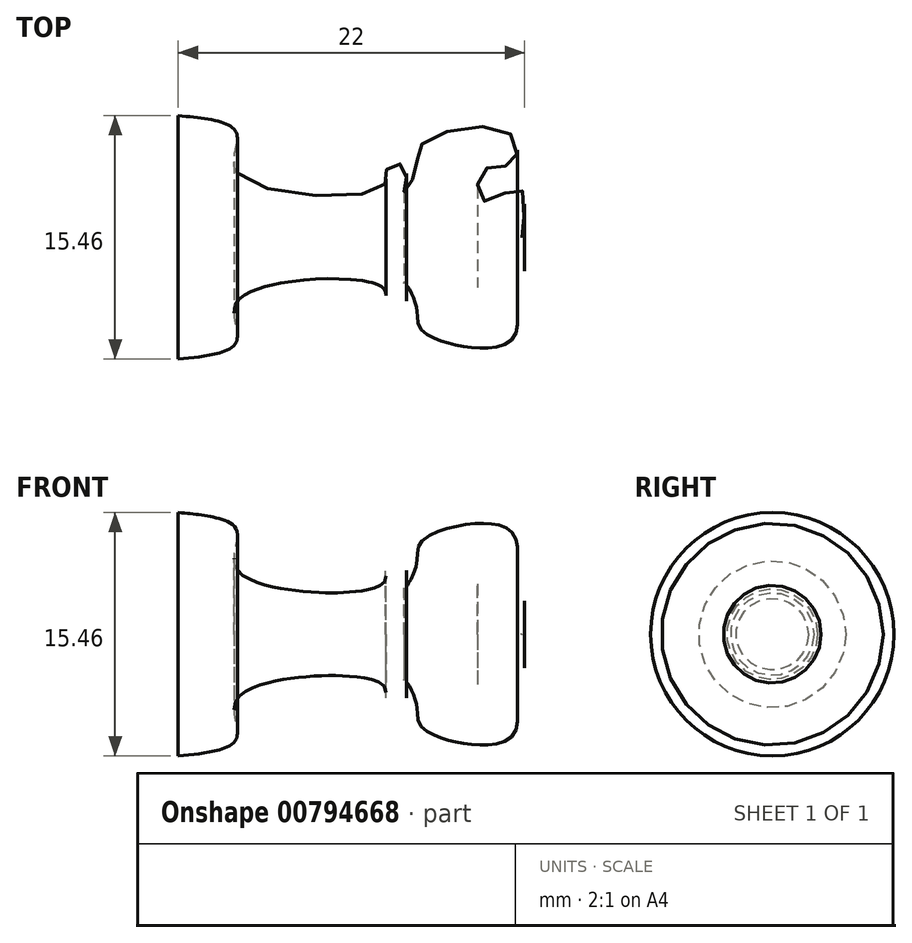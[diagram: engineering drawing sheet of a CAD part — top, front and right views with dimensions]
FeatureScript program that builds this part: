
annotation { "Feature Type Name" : "Feature", "Feature Type Description" : "" }
export const myFeature = defineFeature(function(context is Context, id is Id, definition is map)
    precondition{}
    {
        {
            var Q0;
            Q0=qCreatedBy(makeId("Right.planeOp"),FACE);
            var sketch = newSketch(context, id + "F0", { "sketchPlane" : qUnion([Q0])});
            skCircle(sketch, "E0", {"center": v(0, 0) * mm, "radius": 7.77 * mm});
            skSolve(sketch);
        }
        {
            var Q0;
            Q0=qCreatedBy(makeId("Top.planeOp"),FACE);
            var sketch = newSketch(context, id + "F1", { "sketchPlane" : qUnion([Q0])});
            skFitSpline(sketch, "E1", {"points": [v(0, -7.73) * mm, v(3.72, -6.56) * mm, v(3.84, -3.97) * mm, v(12.98, -3.2) * mm, v(13.25, -4.36) * mm, v(14.42, -4.47) * mm, v(14.34, -2.88) * mm, v(15.11, -4.36) * mm, v(15.54, -5.98) * mm, v(21, -6.64) * mm, v(21.16, -4.67) * mm, v(19.34, -4.24) * mm, v(19.42, -2.3) * mm, v(21.78, -3.04) * mm, v(21.82, 0) * mm, v(21.86, 0) * mm], "startDerivative": vector(59.89, 5.63) * mm, "endDerivative": vector(5.35, -3.35) * mm});
            skLineSegment(sketch, "E2", {"start": v(0, -7.73) * mm, "end": v(0, 0) * mm});
            skLineSegment(sketch, "E3", {"start": v(0, 0) * mm, "end": v(21.86, 0) * mm});
            skSolve(sketch);
        }
        {
            var Q0;
            {var subQ0=sQuery(id+"F1.wireOp",EDGE,"E2");Q0=makeQuery(id+"F1.imprint","IMPRINT",FACE,{"disambiguationData":[TD([[makeQuery(id+"F1.imprint","IMPRINT",EDGE,{"derivedFrom":subQ0}),-1.0]])]});}
            var Q1;
            Q1=sQuery(id+"F0.wireOp",EDGE,"E0");
            sweep(context, id + "F2", {"profiles" : qUnion([Q0]), "path" : qUnion([Q1])});
        }
    });
